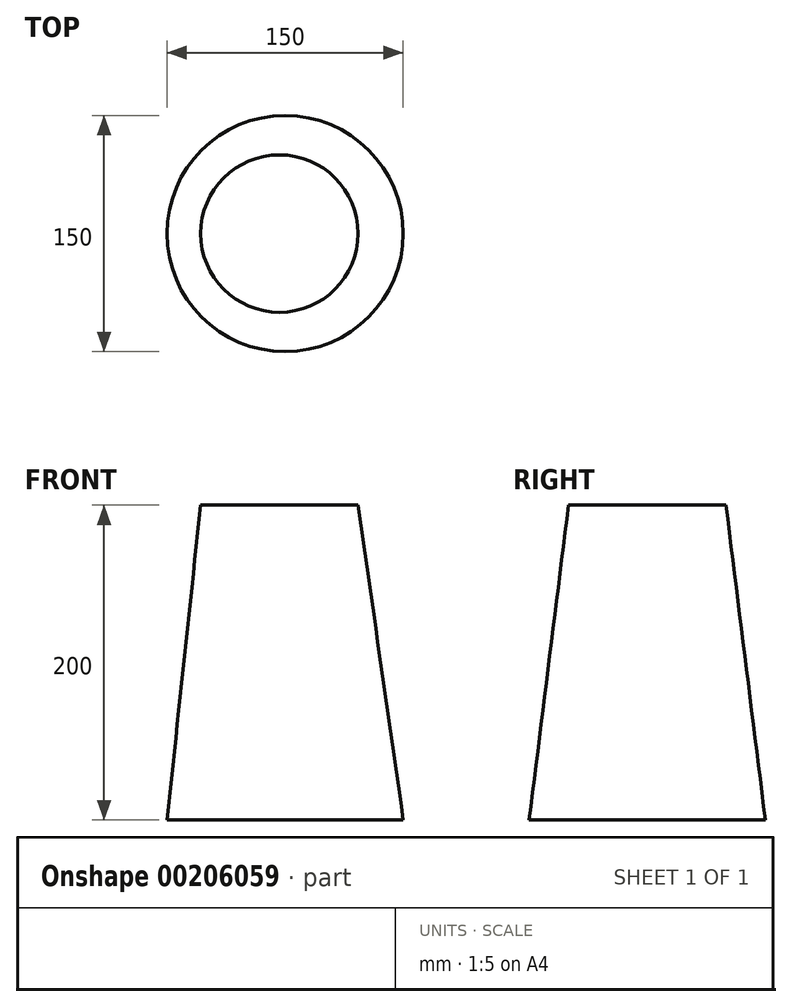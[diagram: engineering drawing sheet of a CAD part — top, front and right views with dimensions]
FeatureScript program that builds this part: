
annotation { "Feature Type Name" : "Feature", "Feature Type Description" : "" }
export const myFeature = defineFeature(function(context is Context, id is Id, definition is map)
    precondition{}
    {
        {
            var Q0;
            Q0=qCreatedBy(makeId("Top.planeOp"),FACE);
            var sketch = newSketch(context, id + "F0", { "sketchPlane" : qUnion([Q0])});
            skCircle(sketch, "E0", {"center": v(3.65, 0) * mm, "radius": 75 * mm});
            skSolve(sketch);
        }
        {
            var Q0;
            Q0=qCreatedBy(makeId("Top.planeOp"),FACE);
            cPlane(context, id + "F1", {"entities" : qUnion([Q0]), "cplaneType" : CPlaneType.OFFSET, "offset" : 200 * mm, "width" : 150 * mm, "height" : 150 * mm});
        }
        {
            var Q0;
            Q0=qCreatedBy(id+"F1.planeOp",FACE);
            var sketch = newSketch(context, id + "F2", { "sketchPlane" : qUnion([Q0])});
            skCircle(sketch, "E1", {"center": v(0, 0) * mm, "radius": 50 * mm});
            skSolve(sketch);
        }
        {
            var Q0;
            Q0=makeQuery(id+"F2.imprint","IMPRINT",FACE,{"disambiguationData":[TD([[makeQuery(id+"F2.imprint","IMPRINT",EDGE,{"derivedFrom":sQuery(id+"F2.wireOp",EDGE,"E1")}),1.0]])]});
            var Q1;
            Q1=makeQuery(id+"F0.imprint","IMPRINT",FACE,{"disambiguationData":[TD([[makeQuery(id+"F0.imprint","IMPRINT",EDGE,{"derivedFrom":sQuery(id+"F0.wireOp",EDGE,"E0")}),1.0]])]});
            loft(context, id + "F3", {"sheetProfilesArray" : [{ "sheetProfileEntities" : qUnion([Q0]) }, { "sheetProfileEntities" : qUnion([Q1]) }]});
        }
    });
